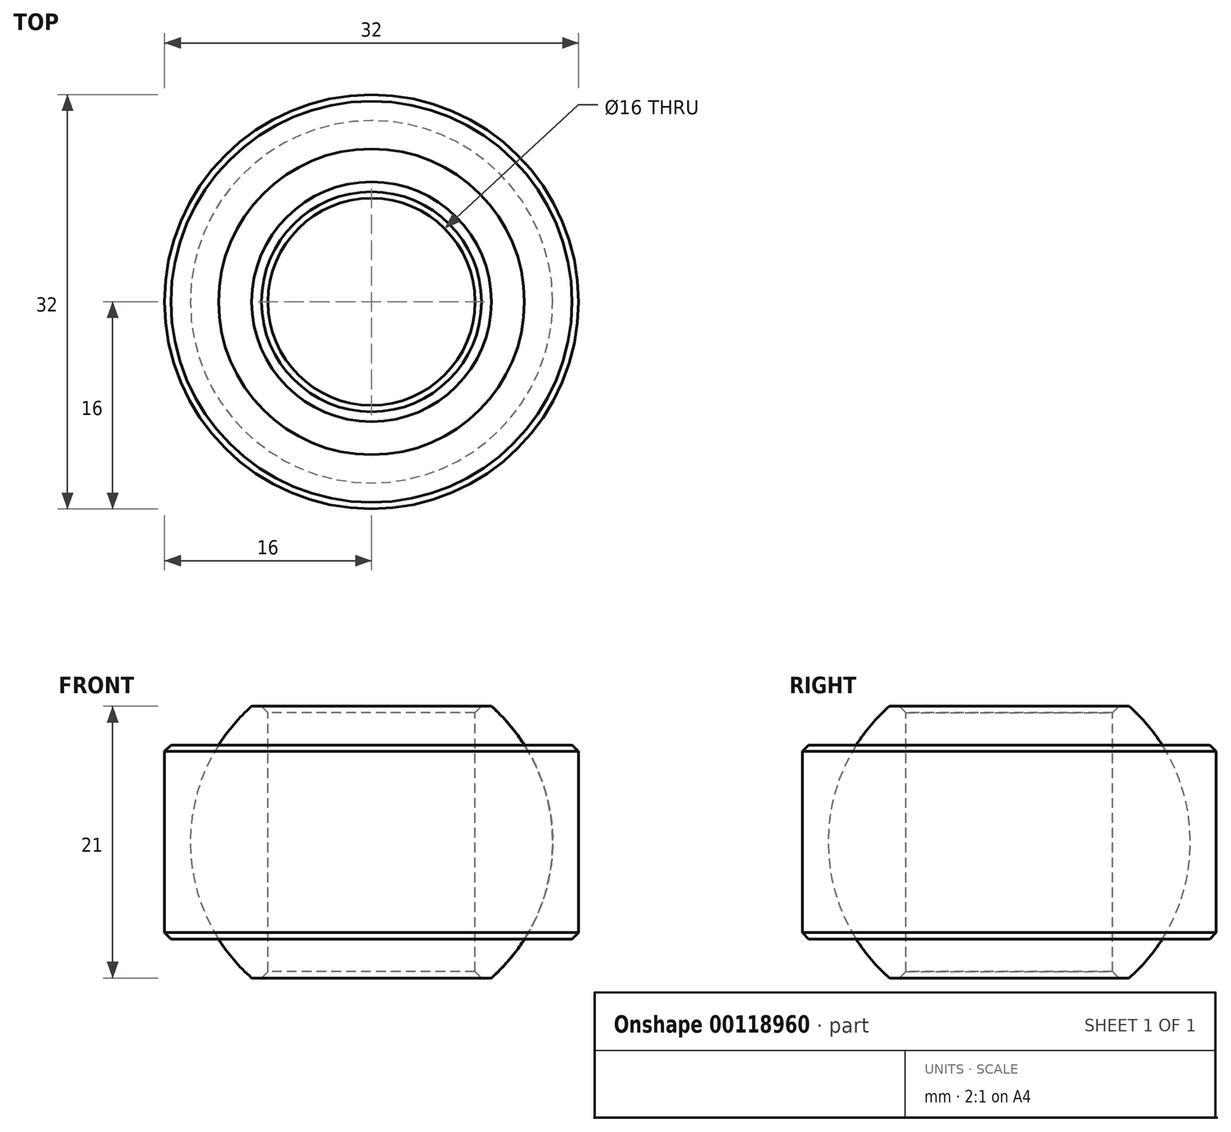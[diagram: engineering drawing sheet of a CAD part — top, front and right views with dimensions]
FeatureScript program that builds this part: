
annotation { "Feature Type Name" : "Feature", "Feature Type Description" : "" }
export const myFeature = defineFeature(function(context is Context, id is Id, definition is map)
    precondition{}
    {
        {
            var Q0;
            Q0=qCreatedBy(makeId("Top.planeOp"),FACE);
            var sketch = newSketch(context, id + "F0", { "sketchPlane" : qUnion([Q0])});
            skCircle(sketch, "E0", {"center": v(0, 0) * mm, "radius": 16 * mm});
            skSolve(sketch);
        }
        {
            var Q0;
            Q0=qSketchRegion(id+"F0",true);
            extrude(context, id + "F1", {"entities" : qUnion([Q0]), "depth" : 15 * mm, "symmetric" : true});
        }
        {
            var Q0;
            Q0=qCreatedBy(makeId("Front.planeOp"),FACE);
            var sketch = newSketch(context, id + "F2", { "sketchPlane" : qUnion([Q0])});
            skCircle(sketch, "E1", {"center": v(0, 0) * mm, "radius": 14 * mm});
            skLineSegment(sketch, "E2", {"start": v(0, -25.5) * mm, "end": v(0, 24.66) * mm});
            skSolve(sketch);
        }
        {
            var Q0;
            {var subQ0=sQuery(id+"F2.wireOp",EDGE,"E2");var subQ1=sQuery(id+"F2.wireOp",EDGE,"E1");var subQ2=makeQuery(id+"F2.imprint","INTERSECT",VERTEX,{"disambiguationData":[OD(0.0)],"derivedFrom":[subQ1,subQ0]});Q0=makeQuery(id+"F2.imprint","IMPRINT",FACE,{"disambiguationData":[TD([[makeQuery(id+"F2.imprint","IMPRINT",EDGE,{"disambiguationData":[TD([[subQ2,-1.0]])],"derivedFrom":subQ1}),1.0]])]});}
            var Q1;
            Q1=sQuery(id+"F2.wireOp",EDGE,"E2");
            revolve(context, id + "F3", {"operationType" : NewBodyOperationType.REMOVE, "entities" : qUnion([Q0]), "axis" : qUnion([Q1]), "revolveType" : RevolveType.FULL, "oppositeDirection" : true});
        }
        {
            var Q0;
            {var subQ0=sQuery(id+"F2.wireOp",EDGE,"E2");var subQ1=sQuery(id+"F2.wireOp",EDGE,"E1");var subQ2=makeQuery(id+"F2.imprint","INTERSECT",VERTEX,{"disambiguationData":[OD(0.0)],"derivedFrom":[subQ1,subQ0]});Q0=makeQuery(id+"F2.imprint","IMPRINT",FACE,{"disambiguationData":[TD([[makeQuery(id+"F2.imprint","IMPRINT",EDGE,{"disambiguationData":[TD([[subQ2,-1.0]])],"derivedFrom":subQ1}),1.0]])]});}
            var Q1;
            Q1=sQuery(id+"F2.wireOp",EDGE,"E2");
            revolve(context, id + "F4", {"entities" : qUnion([Q0]), "axis" : qUnion([Q1]), "revolveType" : RevolveType.FULL});
        }
        {
            var Q0;
            Q0=qCreatedBy(makeId("Front.planeOp"),FACE);
            var sketch = newSketch(context, id + "F5", { "sketchPlane" : qUnion([Q0])});
            skLineSegment(sketch, "E3.bottom", {"start": v(22.57, 10.5) * mm, "end": v(-22.57, 10.5) * mm});
            skLineSegment(sketch, "E3.top", {"start": v(22.57, 31) * mm, "end": v(-22.57, 31) * mm});
            skLineSegment(sketch, "E3.left", {"start": v(22.57, 10.5) * mm, "end": v(22.57, 31) * mm});
            skLineSegment(sketch, "E3.right", {"start": v(-22.57, 10.5) * mm, "end": v(-22.57, 31) * mm});
            skPoint(sketch, "E3.middle", {"position": v(0, 20.75) * mm});
            skLineSegment(sketch, "E4.bottom", {"start": v(20.02, -21.99) * mm, "end": v(-20.02, -21.99) * mm});
            skLineSegment(sketch, "E4.top", {"start": v(20.02, -10.5) * mm, "end": v(-20.02, -10.5) * mm});
            skLineSegment(sketch, "E4.left", {"start": v(20.02, -21.99) * mm, "end": v(20.02, -10.5) * mm});
            skLineSegment(sketch, "E4.right", {"start": v(-20.02, -21.99) * mm, "end": v(-20.02, -10.5) * mm});
            skPoint(sketch, "E4.middle", {"position": v(0, -16.24) * mm});
            skSolve(sketch);
        }
        {
            var Q0;
            Q0=qSketchRegion(id+"F5",true);
            extrude(context, id + "F6", {"entities" : qUnion([Q0]), "operationType" : NewBodyOperationType.REMOVE, "endBound" : BoundingType.THROUGH_ALL, "oppositeDirection" : true, "depth" : 25 * mm, "hasSecondDirection" : true, "secondDirectionBound" : BoundingType.THROUGH_ALL, "secondDirectionOppositeDirection" : false, "secondDirectionDepth" : 25 * mm});
        }
        {
            var Q0;
            Q0=makeQuery(id+"F6.boolean.opBoolean","COPY",FACE,{"derivedFrom":makeQuery(id+"F6.opExtrude","SWEPT_FACE",FACE,{"disambiguationData":[OSD([sQuery(id+"F5.wireOp",EDGE,"E3.bottom")])]})});
            var sketch = newSketch(context, id + "F7", { "sketchPlane" : qUnion([Q0])});
            skCircle(sketch, "E5", {"center": v(0, 0) * mm, "radius": 8 * mm});
            skSolve(sketch);
        }
        {
            var Q0;
            Q0=makeQuery(id+"F7.imprint","IMPRINT",FACE,{"disambiguationData":[TD([[makeQuery(id+"F7.imprint","IMPRINT",EDGE,{"derivedFrom":sQuery(id+"F7.wireOp",EDGE,"E5")}),1.0]])]});
            extrude(context, id + "F8", {"entities" : qUnion([Q0]), "operationType" : NewBodyOperationType.REMOVE, "endBound" : BoundingType.THROUGH_ALL, "oppositeDirection" : true, "depth" : 25 * mm});
        }
        {
            var Q0;
            Q0=makeQuery(id+"F8.boolean.opBoolean","COPY",FACE,{"derivedFrom":makeQuery(id+"F8.opExtrude","SWEPT_FACE",FACE,{"disambiguationData":[OSD([sQuery(id+"F7.wireOp",EDGE,"E5")])]})});
            var Q1;
            Q1=makeQuery(id+"F1.opExtrude","SWEPT_FACE",FACE,{"disambiguationData":[OSD([sQuery(id+"F0.wireOp",EDGE,"E0")])]});
            chamfer(context, id + "F9", {"entities" : qUnion([Q0, Q1]), "width" : 0.5 * mm, "tangentPropagation" : true});
        }
    });
